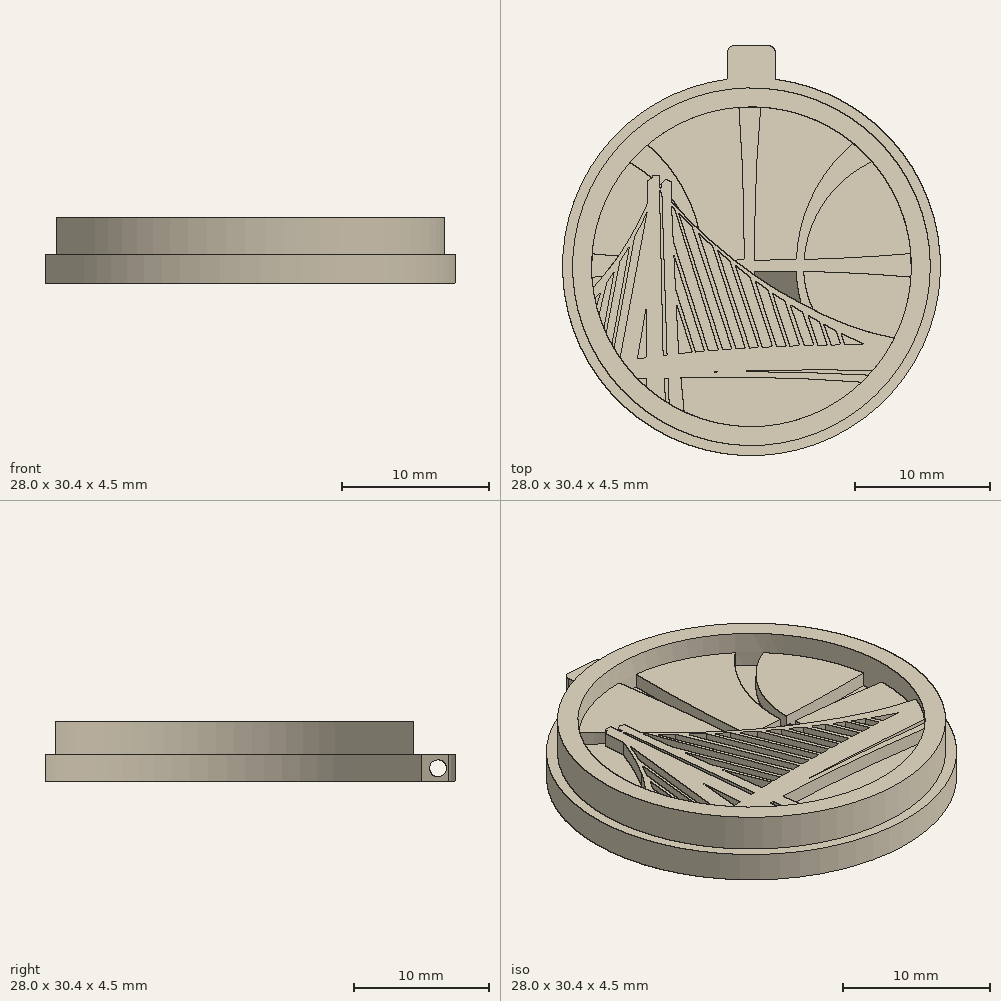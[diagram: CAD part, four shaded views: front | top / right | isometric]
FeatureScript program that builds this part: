
annotation { "Feature Type Name" : "Feature", "Feature Type Description" : "" }
export const myFeature = defineFeature(function(context is Context, id is Id, definition is map)
    precondition{}
    {
        {
            var Q0;
            Q0=qCreatedBy(makeId("Top.planeOp"),FACE);
            var sketch = newSketch(context, id + "F0", { "sketchPlane" : qUnion([Q0])});
            skCircle(sketch, "E0", {"center": v(0, 0) * mm, "radius": 12.5 * mm});
            skCircle(sketch, "E1", {"center": v(0, 0) * mm, "radius": 14 * mm});
            skSolve(sketch);
        }
        {
            var Q0;
            Q0 = qSketchRegion(id + "F0", true);
            var Q1;
            Q1=makeQuery(id+"F0.imprint","IMPRINT",FACE,{"disambiguationData":[TD([[makeQuery(id+"F0.imprint","IMPRINT",EDGE,{"derivedFrom":sQuery(id+"F0.wireOp",EDGE,"E0")}),1.0]])]});
            extrude(context, id + "F1", {"entities" : qUnion([Q0, Q1]), "depth" : 2 * mm, "offsetDistance" : 25 * mm});
        }
        {
            var Q0;
            Q0=makeQuery(id+"F1.opExtrude","CAP_FACE",FACE,{"disambiguationData":[OSD([sQuery(id+"F0.wireOp",EDGE,"E1")])],"isStart":false});
            var sketch = newSketch(context, id + "F2", { "sketchPlane" : qUnion([Q0])});
            skCircle(sketch, "E2", {"center": v(0, 0) * mm, "radius": 11.85 * mm});
            skArc(sketch, "E3", {"start": v(-0.54, 0.5) * mm, "mid": v(-0.63, 6.16) * mm, "end": v(-0.93, 11.81) * mm});
            skArc(sketch, "E4", {"start": v(0.69, 11.83) * mm, "mid": v(0.32, 6.17) * mm, "end": v(0.24, 0.5) * mm});
            skArc(sketch, "E5", {"start": v(0.24, 0.5) * mm, "mid": v(1.78, 0.5) * mm, "end": v(3.32, 0.52) * mm});
            skArc(sketch, "E6", {"start": v(11.82, -0.77) * mm, "mid": v(7.85, -0.49) * mm, "end": v(3.86, -0.34) * mm});
            skArc(sketch, "E7", {"start": v(8.94, 7.78) * mm, "mid": v(5.45, 4.83) * mm, "end": v(3.9, 0.54) * mm});
            skArc(sketch, "E8", {"start": v(7.55, 9.13) * mm, "mid": v(4.52, 5.28) * mm, "end": v(3.32, 0.52) * mm});
            skArc(sketch, "E9", {"start": v(-3.88, 2.71) * mm, "mid": v(-5.28, 6.17) * mm, "end": v(-7.68, 9.02) * mm});
            skArc(sketch, "E10", {"start": v(-5.28, 4.12) * mm, "mid": v(-5.59, 4.6) * mm, "end": v(-5.92, 5.04) * mm});
            skPoint(sketch, "E10.startSnap0", {"position": v(-5.28, 6.17) * mm});
            skArc(sketch, "E11", {"start": v(-5.28, 4.12) * mm, "mid": v(-3.36, 2.23) * mm, "end": v(-1.3, 0.5) * mm});
            skLineSegment(sketch, "E12", {"start": v(-0.54, 0.5) * mm, "end": v(-1.3, 0.5) * mm});
            skLineSegment(sketch, "E13", {"start": v(-11.82, -0.77) * mm, "end": v(-11, -0.73) * mm});
            skLineSegment(sketch, "E14", {"start": v(-11.81, 0.96) * mm, "end": v(-9.83, 0.79) * mm});
            skArc(sketch, "E15", {"start": v(-11, -0.73) * mm, "mid": v(-10.4, 0.02) * mm, "end": v(-9.83, 0.79) * mm});
            skLineSegment(sketch, "E16", {"start": v(-7.36, 6.55) * mm, "end": v(-7.36, 6.75) * mm});
            skLineSegment(sketch, "E17", {"start": v(-7.36, 6.75) * mm, "end": v(-6.8, 6.75) * mm});
            skLineSegment(sketch, "E18", {"start": v(-6.8, 6.75) * mm, "end": v(-6.8, 6.03) * mm});
            skLineSegment(sketch, "E19", {"start": v(-6.8, 6.03) * mm, "end": v(-6.32, 6.45) * mm});
            skLineSegment(sketch, "E20", {"start": v(-6.32, 6.45) * mm, "end": v(-5.92, 6.3) * mm});
            skLineSegment(sketch, "E21", {"start": v(-5.92, 6.3) * mm, "end": v(-5.92, 5.04) * mm});
            skArc(sketch, "E22.trimOffspring", {"start": v(-7.36, 6.55) * mm, "mid": v(-8.16, 7.17) * mm, "end": v(-9, 7.7) * mm});
            skArc(sketch, "E23", {"start": v(3.86, -0.34) * mm, "mid": v(4.07, -1.78) * mm, "end": v(4.56, -3.14) * mm});
            skArc(sketch, "E24", {"start": v(3.33, -0.33) * mm, "mid": v(3.42, -1.53) * mm, "end": v(3.67, -2.7) * mm});
            skArc(sketch, "E25", {"start": v(3.67, -2.7) * mm, "mid": v(4.1, -2.94) * mm, "end": v(4.56, -3.14) * mm});
            skArc(sketch, "E26.trimOffspring", {"start": v(3.9, 0.54) * mm, "mid": v(7.86, 0.7) * mm, "end": v(11.8, 0.97) * mm});
            skArc(sketch, "E27.trimOffspring", {"start": v(3.33, -0.33) * mm, "mid": v(1.79, -0.32) * mm, "end": v(0.24, -0.34) * mm});
            skArc(sketch, "E28", {"start": v(-1.3, 0.5) * mm, "mid": v(-0.54, -0.1) * mm, "end": v(0.24, -0.63) * mm});
            skLineSegment(sketch, "E29", {"start": v(0.24, -0.34) * mm, "end": v(0.24, -0.63) * mm});
            skSolve(sketch);
        }
        {
            var Q0;
            {var subQ1=sQuery(id+"F2.wireOp",EDGE,"E3");Q0=makeQuery(id+"F2.imprint","IMPRINT",FACE,{"disambiguationData":[TD([[makeQuery(id+"F2.imprint","IMPRINT",EDGE,{"derivedFrom":subQ1}),1.0]])]});}
            var Q1;
            {var subQ0=sQuery(id+"F2.wireOp",EDGE,"E4");Q1=makeQuery(id+"F2.imprint","IMPRINT",FACE,{"disambiguationData":[TD([[makeQuery(id+"F2.imprint","IMPRINT",EDGE,{"derivedFrom":subQ0}),1.0]])]});}
            var Q2;
            {var subQ0=sQuery(id+"F2.wireOp",EDGE,"E7");Q2=makeQuery(id+"F2.imprint","IMPRINT",FACE,{"disambiguationData":[TD([[makeQuery(id+"F2.imprint","IMPRINT",EDGE,{"derivedFrom":subQ0}),1.0]])]});}
            var Q3;
            {var subQ6=sQuery(id+"F2.wireOp",EDGE,"E6");Q3=makeQuery(id+"F2.imprint","IMPRINT",FACE,{"disambiguationData":[TD([[makeQuery(id+"F2.imprint","IMPRINT",EDGE,{"derivedFrom":subQ6}),1.0]])]});}
            extrude(context, id + "F3", {"entities" : qUnion([Q0, Q1, Q2, Q3]), "operationType" : NewBodyOperationType.ADD, "depth" : 1 * mm, "offsetDistance" : 25 * mm});
        }
        {
            var Q0;
            Q0=makeQuery(id+"F1.opExtrude","CAP_FACE",FACE,{"disambiguationData":[OSD([sQuery(id+"F0.wireOp",EDGE,"E1")])],"isStart":false});
            var sketch = newSketch(context, id + "F4", { "sketchPlane" : qUnion([Q0])});
            skCircle(sketch, "E30.0", {"center": v(0, 0) * mm, "radius": 13.25 * mm});
            skCircle(sketch, "E31", {"center": v(0, 0) * mm, "radius": 11.85 * mm});
            skSolve(sketch);
        }
        {
            var Q0;
            Q0 = qSketchRegion(id + "F4", true);
            extrude(context, id + "F5", {"entities" : qUnion([Q0]), "operationType" : NewBodyOperationType.ADD, "depth" : 2 * mm, "offsetDistance" : 25 * mm});
        }
        {
            var Q0;
            Q0=makeQuery(id+"F3.opExtrude","CAP_FACE",FACE,{"disambiguationData":[OSD([sQuery(id+"F2.wireOp",EDGE,"E2"),sQuery(id+"F2.wireOp",EDGE,"E3"),sQuery(id+"F2.wireOp",EDGE,"E6"),sQuery(id+"F2.wireOp",EDGE,"E9"),sQuery(id+"F2.wireOp",EDGE,"E10"),sQuery(id+"F2.wireOp",EDGE,"E11"),sQuery(id+"F2.wireOp",EDGE,"E12"),sQuery(id+"F2.wireOp",EDGE,"E13"),sQuery(id+"F2.wireOp",EDGE,"E14"),sQuery(id+"F2.wireOp",EDGE,"E15"),sQuery(id+"F2.wireOp",EDGE,"E16"),sQuery(id+"F2.wireOp",EDGE,"E17"),sQuery(id+"F2.wireOp",EDGE,"E18"),sQuery(id+"F2.wireOp",EDGE,"E19"),sQuery(id+"F2.wireOp",EDGE,"E20"),sQuery(id+"F2.wireOp",EDGE,"E21"),sQuery(id+"F2.wireOp",EDGE,"E22.trimOffspring"),sQuery(id+"F2.wireOp",EDGE,"E23"),sQuery(id+"F2.wireOp",EDGE,"E24"),sQuery(id+"F2.wireOp",EDGE,"E25"),sQuery(id+"F2.wireOp",EDGE,"E27.trimOffspring"),sQuery(id+"F2.wireOp",EDGE,"E28"),sQuery(id+"F2.wireOp",EDGE,"E29")])],"isStart":false});
            var sketch = newSketch(context, id + "F6", { "sketchPlane" : qUnion([Q0])});
            skLineSegment(sketch, "E32", {"start": v(-7.81, -6.75) * mm, "end": v(-7.81, -3.1) * mm});
            skLineSegment(sketch, "E33", {"start": v(-7.81, -3.1) * mm, "end": v(-8.45, -6.81) * mm});
            skLineSegment(sketch, "E34", {"start": v(-8.45, -6.81) * mm, "end": v(-7.81, -6.75) * mm});
            skLineSegment(sketch, "E35", {"start": v(-11.48, -2.94) * mm, "end": v(-11.15, -1.87) * mm});
            skLineSegment(sketch, "E36", {"start": v(-11.15, -1.87) * mm, "end": v(-11.6, -2.39) * mm});
            skLineSegment(sketch, "E37", {"start": v(-11.3, -3.59) * mm, "end": v(-10.7, -1.17) * mm});
            skLineSegment(sketch, "E38", {"start": v(-10.7, -1.17) * mm, "end": v(-10.16, -0.36) * mm});
            skLineSegment(sketch, "E39", {"start": v(-10.16, -0.36) * mm, "end": v(-10.93, -4.58) * mm});
            skLineSegment(sketch, "E40", {"start": v(-11.74, -1.6) * mm, "end": v(-11, -0.73) * mm});
            skArc(sketch, "E41", {"start": v(-9.83, 0.79) * mm, "mid": v(-8.68, 2.68) * mm, "end": v(-7.7, 4.66) * mm});
            skLineSegment(sketch, "E42", {"start": v(-7.7, 4.66) * mm, "end": v(-7.7, 6.36) * mm});
            skLineSegment(sketch, "E43", {"start": v(-7.7, 6.36) * mm, "end": v(-7.36, 6.55) * mm});
            skLineSegment(sketch, "E44", {"start": v(-7.36, 6.55) * mm, "end": v(-7.36, 6.75) * mm});
            skLineSegment(sketch, "E45", {"start": v(-7.36, 6.75) * mm, "end": v(-6.8, 6.75) * mm});
            skLineSegment(sketch, "E46", {"start": v(-6.8, 6.75) * mm, "end": v(-6.8, 5.88) * mm});
            skLineSegment(sketch, "E47", {"start": v(-6.8, 5.88) * mm, "end": v(-6.64, 5.71) * mm});
            skLineSegment(sketch, "E48", {"start": v(-6.64, 5.71) * mm, "end": v(-6.64, 6.18) * mm});
            skLineSegment(sketch, "E49", {"start": v(-6.64, 6.18) * mm, "end": v(-6.32, 6.45) * mm});
            skLineSegment(sketch, "E50", {"start": v(-6.32, 6.45) * mm, "end": v(-5.92, 6.3) * mm});
            skLineSegment(sketch, "E51", {"start": v(-5.92, 6.3) * mm, "end": v(-5.92, 4.8) * mm});
            skArc(sketch, "E52", {"start": v(-5.92, 4.8) * mm, "mid": v(-3.7, 2.55) * mm, "end": v(-1.3, 0.5) * mm});
            skArc(sketch, "E53", {"start": v(-1.3, 0.5) * mm, "mid": v(1.1, -1.23) * mm, "end": v(3.67, -2.7) * mm});
            skArc(sketch, "E54", {"start": v(3.67, -2.7) * mm, "mid": v(7.03, -4.28) * mm, "end": v(10.6, -5.3) * mm});
            skLineSegment(sketch, "E55", {"start": v(-6.47, -8.27) * mm, "end": v(-6.37, -10) * mm});
            skLineSegment(sketch, "E56", {"start": v(-6.47, -8.27) * mm, "end": v(-6.18, -8.27) * mm});
            skLineSegment(sketch, "E57", {"start": v(-6.18, -8.27) * mm, "end": v(-6.1, -10.16) * mm});
            skLineSegment(sketch, "E58", {"start": v(-7.8, -8.92) * mm, "end": v(-7.8, -8.3) * mm});
            skLineSegment(sketch, "E59", {"start": v(-7.8, -8.3) * mm, "end": v(-8.46, -8.3) * mm});
            skArc(sketch, "E60", {"start": v(8.2, -8.55) * mm, "mid": v(1.5, -8.21) * mm, "end": v(-5.23, -8.24) * mm});
            skArc(sketch, "E61", {"start": v(8.71, -8.03) * mm, "mid": v(2.98, -7.82) * mm, "end": v(-2.77, -7.8) * mm});
            skArc(sketch, "E62", {"start": v(9.03, -7.68) * mm, "mid": v(3.13, -7.65) * mm, "end": v(-2.77, -7.8) * mm});
            skArc(sketch, "E63", {"start": v(8.48, -5.79) * mm, "mid": v(7.7, -5.79) * mm, "end": v(6.91, -5.8) * mm});
            skArc(sketch, "E64", {"start": v(-5.92, 4.51) * mm, "mid": v(-5.8, 4.38) * mm, "end": v(-5.68, 4.26) * mm});
            skLineSegment(sketch, "E65", {"start": v(-5.92, 4.51) * mm, "end": v(-5.8, 1.88) * mm});
            skLineSegment(sketch, "E66", {"start": v(-6.26, -6.55) * mm, "end": v(-6.64, 5.45) * mm});
            skPoint(sketch, "E66.endSnap0", {"position": v(-6.64, 5.94) * mm});
            skLineSegment(sketch, "E67", {"start": v(-6.64, 5.45) * mm, "end": v(-6.82, 5.65) * mm});
            skLineSegment(sketch, "E68", {"start": v(-6.82, 5.65) * mm, "end": v(-6.55, -6.57) * mm});
            skLineSegment(sketch, "E69", {"start": v(-6.55, -6.57) * mm, "end": v(-6.26, -6.55) * mm});
            skLineSegment(sketch, "E70", {"start": v(-8.73, -6.88) * mm, "end": v(-7.78, -1.6) * mm});
            skLineSegment(sketch, "E71", {"start": v(-7.78, -1.6) * mm, "end": v(-7.7, 2.5) * mm});
            skLineSegment(sketch, "E72", {"start": v(-7.7, 2.5) * mm, "end": v(-9.56, -7) * mm});
            skLineSegment(sketch, "E73", {"start": v(-9.56, -7) * mm, "end": v(-8.73, -6.88) * mm});
            skArc(sketch, "E74", {"start": v(-9.76, 0.35) * mm, "mid": v(-9.39, 0.94) * mm, "end": v(-9.03, 1.54) * mm});
            skLineSegment(sketch, "E75", {"start": v(-7.73, 4.03) * mm, "end": v(-9.73, -6.77) * mm});
            skLineSegment(sketch, "E76", {"start": v(-10.18, -6.06) * mm, "end": v(-8.66, 2.18) * mm});
            skLineSegment(sketch, "E77", {"start": v(-9.03, 1.54) * mm, "end": v(-10.34, -5.79) * mm});
            skLineSegment(sketch, "E78", {"start": v(-9.76, 0.35) * mm, "end": v(-10.77, -4.95) * mm});
            skArc(sketch, "E79.trimOffspring", {"start": v(-8.66, 2.18) * mm, "mid": v(-8.18, 3.1) * mm, "end": v(-7.73, 4.03) * mm});
            skArc(sketch, "E80", {"start": v(-11.74, -1.6) * mm, "mid": v(-11.68, -2) * mm, "end": v(-11.6, -2.39) * mm});
            skLineSegment(sketch, "E81", {"start": v(-5.23, -8.24) * mm, "end": v(-4.99, -10.75) * mm});
            skLineSegment(sketch, "E82", {"start": v(-5.58, -2.66) * mm, "end": v(-4.39, -6.34) * mm});
            skLineSegment(sketch, "E83", {"start": v(-3.47, -6.26) * mm, "end": v(-5.75, 0.89) * mm});
            skLineSegment(sketch, "E84", {"start": v(-5.63, -1.66) * mm, "end": v(-4.16, -6.32) * mm});
            skLineSegment(sketch, "E85", {"start": v(-3.19, -6.24) * mm, "end": v(-5.8, 1.88) * mm});
            skLineSegment(sketch, "E86", {"start": v(-5.68, 4.26) * mm, "end": v(-2.45, -6.18) * mm});
            skLineSegment(sketch, "E87", {"start": v(-2.13, -6.16) * mm, "end": v(-5.4, 3.95) * mm});
            skLineSegment(sketch, "E88", {"start": v(-4.4, 2.94) * mm, "end": v(-1.45, -6.11) * mm});
            skLineSegment(sketch, "E89", {"start": v(-1.15, -6.09) * mm, "end": v(-3.9, 2.46) * mm});
            skLineSegment(sketch, "E90", {"start": v(-2.88, 1.52) * mm, "end": v(-0.46, -6.05) * mm});
            skLineSegment(sketch, "E91", {"start": v(-2.5, 1.2) * mm, "end": v(-0.14, -6.03) * mm});
            skLineSegment(sketch, "E92", {"start": v(0.54, -5.99) * mm, "end": v(-1.6, 0.42) * mm});
            skLineSegment(sketch, "E93", {"start": v(-1.2, 0.1) * mm, "end": v(0.81, -5.97) * mm});
            skLineSegment(sketch, "E94", {"start": v(1.87, -5.92) * mm, "end": v(0.26, -1.03) * mm});
            skLineSegment(sketch, "E95", {"start": v(1.56, -5.94) * mm, "end": v(-0.14, -0.73) * mm});
            skLineSegment(sketch, "E96", {"start": v(2.57, -5.9) * mm, "end": v(1.2, -1.7) * mm});
            skLineSegment(sketch, "E97", {"start": v(1.54, -1.94) * mm, "end": v(2.84, -5.88) * mm});
            skLineSegment(sketch, "E98", {"start": v(3.58, -5.86) * mm, "end": v(2.48, -2.56) * mm});
            skLineSegment(sketch, "E99", {"start": v(3.92, -5.85) * mm, "end": v(2.85, -2.8) * mm});
            skLineSegment(sketch, "E100", {"start": v(4.18, -3.6) * mm, "end": v(4.91, -5.82) * mm});
            skLineSegment(sketch, "E101", {"start": v(3.8, -3.37) * mm, "end": v(4.62, -5.83) * mm});
            skLineSegment(sketch, "E102", {"start": v(5.62, -5.8) * mm, "end": v(5.02, -4.07) * mm});
            skLineSegment(sketch, "E103", {"start": v(5.9, -5.8) * mm, "end": v(5.35, -4.25) * mm});
            skLineSegment(sketch, "E104", {"start": v(6.25, -4.73) * mm, "end": v(6.61, -5.8) * mm});
            skLineSegment(sketch, "E105", {"start": v(6.61, -4.91) * mm, "end": v(6.91, -5.8) * mm});
            skArc(sketch, "E106.trimOffspring", {"start": v(-3.9, 2.46) * mm, "mid": v(-3.4, 1.99) * mm, "end": v(-2.88, 1.52) * mm});
            skArc(sketch, "E107.trimOffspring", {"start": v(-2.5, 1.2) * mm, "mid": v(-2.05, 0.8) * mm, "end": v(-1.6, 0.42) * mm});
            skArc(sketch, "E108.trimOffspring", {"start": v(-5.4, 3.95) * mm, "mid": v(-4.9, 3.44) * mm, "end": v(-4.4, 2.94) * mm});
            skArc(sketch, "E109.trimOffspring", {"start": v(-1.2, 0.1) * mm, "mid": v(-0.68, -0.32) * mm, "end": v(-0.14, -0.73) * mm});
            skArc(sketch, "E110.trimOffspring", {"start": v(0.26, -1.03) * mm, "mid": v(0.73, -1.36) * mm, "end": v(1.2, -1.7) * mm});
            skArc(sketch, "E111.trimOffspring", {"start": v(1.54, -1.94) * mm, "mid": v(2, -2.25) * mm, "end": v(2.48, -2.56) * mm});
            skArc(sketch, "E112.trimOffspring", {"start": v(4.18, -3.6) * mm, "mid": v(4.6, -3.84) * mm, "end": v(5.02, -4.07) * mm});
            skArc(sketch, "E113.trimOffspring", {"start": v(2.85, -2.8) * mm, "mid": v(3.32, -3.08) * mm, "end": v(3.8, -3.37) * mm});
            skArc(sketch, "E114.trimOffspring", {"start": v(5.35, -4.25) * mm, "mid": v(5.8, -4.5) * mm, "end": v(6.25, -4.73) * mm});
            skArc(sketch, "E115.trimOffspring", {"start": v(6.61, -4.91) * mm, "mid": v(7.54, -5.36) * mm, "end": v(8.48, -5.79) * mm});
            skArc(sketch, "E116.trimOffspring", {"start": v(6.61, -5.8) * mm, "mid": v(6.26, -5.8) * mm, "end": v(5.9, -5.8) * mm});
            skArc(sketch, "E117.trimOffspring", {"start": v(5.62, -5.8) * mm, "mid": v(5.27, -5.81) * mm, "end": v(4.91, -5.82) * mm});
            skArc(sketch, "E118.trimOffspring", {"start": v(4.62, -5.83) * mm, "mid": v(4.27, -5.84) * mm, "end": v(3.92, -5.85) * mm});
            skArc(sketch, "E119.trimOffspring", {"start": v(3.58, -5.86) * mm, "mid": v(3.21, -5.87) * mm, "end": v(2.84, -5.88) * mm});
            skArc(sketch, "E120.trimOffspring", {"start": v(1.56, -5.94) * mm, "mid": v(1.19, -5.95) * mm, "end": v(0.81, -5.97) * mm});
            skArc(sketch, "E121.trimOffspring", {"start": v(2.57, -5.9) * mm, "mid": v(2.22, -5.9) * mm, "end": v(1.87, -5.92) * mm});
            skArc(sketch, "E122.trimOffspring", {"start": v(-2.45, -6.18) * mm, "mid": v(-2.82, -6.21) * mm, "end": v(-3.19, -6.24) * mm});
            skArc(sketch, "E123.trimOffspring", {"start": v(-1.45, -6.11) * mm, "mid": v(-1.79, -6.13) * mm, "end": v(-2.13, -6.16) * mm});
            skArc(sketch, "E124.trimOffspring", {"start": v(-3.47, -6.26) * mm, "mid": v(-3.81, -6.3) * mm, "end": v(-4.16, -6.32) * mm});
            skArc(sketch, "E125.trimOffspring", {"start": v(0.54, -5.99) * mm, "mid": v(0.2, -6) * mm, "end": v(-0.14, -6.03) * mm});
            skArc(sketch, "E126.trimOffspring", {"start": v(-0.46, -6.05) * mm, "mid": v(-0.8, -6.07) * mm, "end": v(-1.15, -6.09) * mm});
            skArc(sketch, "E127.trimOffspring", {"start": v(-4.39, -6.34) * mm, "mid": v(-4.9, -6.4) * mm, "end": v(-5.4, -6.44) * mm});
            skLineSegment(sketch, "E128.trimOffspring", {"start": v(-5.58, -2.66) * mm, "end": v(-5.4, -6.44) * mm});
            skLineSegment(sketch, "E129.trimOffspring", {"start": v(-5.75, 0.89) * mm, "end": v(-5.63, -1.66) * mm});
            skArc(sketch, "E130.trimOffspring", {"start": v(8.2, -8.55) * mm, "mid": v(8.46, -8.3) * mm, "end": v(8.71, -8.03) * mm});
            skArc(sketch, "E131.trimOffspring", {"start": v(9.03, -7.68) * mm, "mid": v(9.88, -6.54) * mm, "end": v(10.6, -5.3) * mm});
            skArc(sketch, "E132.trimOffspring", {"start": v(-6.1, -10.16) * mm, "mid": v(-5.55, -10.47) * mm, "end": v(-4.99, -10.75) * mm});
            skArc(sketch, "E133.trimOffspring", {"start": v(-7.8, -8.92) * mm, "mid": v(-7.1, -9.48) * mm, "end": v(-6.37, -10) * mm});
            skArc(sketch, "E134.trimOffspring", {"start": v(-11.48, -2.94) * mm, "mid": v(-11.4, -3.27) * mm, "end": v(-11.3, -3.59) * mm});
            skArc(sketch, "E135.trimOffspring", {"start": v(-10.93, -4.58) * mm, "mid": v(-10.85, -4.76) * mm, "end": v(-10.77, -4.95) * mm});
            skArc(sketch, "E136.trimOffspring", {"start": v(-10.34, -5.79) * mm, "mid": v(-10.26, -5.92) * mm, "end": v(-10.18, -6.06) * mm});
            skArc(sketch, "E137.trimOffspring", {"start": v(-9.73, -6.77) * mm, "mid": v(-9.13, -7.56) * mm, "end": v(-8.46, -8.3) * mm});
            skArc(sketch, "E138", {"start": v(-11, -0.73) * mm, "mid": v(-10.4, 0.02) * mm, "end": v(-9.83, 0.79) * mm});
            skSolve(sketch);
        }
        {
            var Q0;
            Q0 = qSketchRegion(id + "F6", true);
            extrude(context, id + "F7", {"entities" : qUnion([Q0]), "depth" : 1 * mm, "offsetDistance" : 25 * mm});
        }
        {
            var Q0;
            Q0=makeQuery(id+"F1.opExtrude","CAP_FACE",FACE,{"disambiguationData":[OSD([sQuery(id+"F0.wireOp",EDGE,"E1")])],"isStart":false});
            var sketch = newSketch(context, id + "F8", { "sketchPlane" : qUnion([Q0])});
            skLineSegment(sketch, "E139.top", {"start": v(-1.75, 16.4) * mm, "end": v(1.75, 16.4) * mm});
            skLineSegment(sketch, "E139.left", {"start": v(-1.75, 13.9) * mm, "end": v(-1.75, 16.4) * mm});
            skLineSegment(sketch, "E139.right", {"start": v(1.75, 13.9) * mm, "end": v(1.75, 16.4) * mm});
            skPoint(sketch, "E139.middle", {"position": v(0, 15.14) * mm});
            skLineSegment(sketch, "E140", {"start": v(0, 15.14) * mm, "end": v(0, 0) * mm, "construction": true});
            skArc(sketch, "E141", {"start": v(-1.75, 13.9) * mm, "mid": v(0, 13.87) * mm, "end": v(1.75, 13.9) * mm});
            skSolve(sketch);
        }
        {
            var Q0;
            Q0 = qSketchRegion(id + "F8", true);
            extrude(context, id + "F9", {"entities" : qUnion([Q0]), "operationType" : NewBodyOperationType.ADD, "oppositeDirection" : true, "depth" : 2 * mm, "offsetDistance" : 25 * mm});
        }
        {
            var Q0;
            Q0=makeQuery(id+"F9.opExtrude","SWEPT_EDGE",EDGE,{"disambiguationData":[OSD([sQuery(id+"F8.wireOp",EDGE,"E139.top"),sQuery(id+"F8.wireOp",EDGE,"E139.right")])]});
            var Q1;
            Q1=makeQuery(id+"F9.opExtrude","SWEPT_EDGE",EDGE,{"disambiguationData":[OSD([sQuery(id+"F0.wireOp",EDGE,"E1"),sQuery(id+"F8.wireOp",EDGE,"E139.right"),sQuery(id+"F8.wireOp",EDGE,"E141")])]});
            var Q2;
            Q2=makeQuery(id+"F9.opExtrude","SWEPT_EDGE",EDGE,{"disambiguationData":[OSD([sQuery(id+"F8.wireOp",EDGE,"E139.top"),sQuery(id+"F8.wireOp",EDGE,"E139.left")])]});
            var Q3;
            Q3=makeQuery(id+"F9.opExtrude","SWEPT_EDGE",EDGE,{"disambiguationData":[OSD([sQuery(id+"F0.wireOp",EDGE,"E1"),sQuery(id+"F8.wireOp",EDGE,"E139.left"),sQuery(id+"F8.wireOp",EDGE,"E141")])]});
            fillet(context, id + "F10", {"entities" : qUnion([Q0, Q1, Q2, Q3]), "radius" : .5 * mm, "tangentPropagation" : true, "allowEdgeOverflow" : false});
        }
        {
            var Q0;
            Q0=makeQuery(id+"F9.opExtrude","SWEPT_FACE",FACE,{"disambiguationData":[OSD([sQuery(id+"F8.wireOp",EDGE,"E139.right")])]});
            var sketch = newSketch(context, id + "F11", { "sketchPlane" : qUnion([Q0])});
            skCircle(sketch, "E142", {"center": v(15.1, 1) * mm, "radius": 0.62 * mm});
            skPoint(sketch, "E142.centerSnap0", {"position": v(14.32, 1) * mm});
            skPoint(sketch, "E142.centerSnap1", {"position": v(15.1, 2) * mm});
            skSolve(sketch);
        }
        {
            var Q0;
            Q0 = qSketchRegion(id + "F11", true);
            extrude(context, id + "F12", {"entities" : qUnion([Q0]), "operationType" : NewBodyOperationType.REMOVE, "oppositeDirection" : true, "depth" : 25 * mm, "offsetDistance" : 25 * mm, "hasSecondDirection" : true, "secondDirectionOppositeDirection" : false, "secondDirectionDepth" : 25 * mm});
        }
        {
            var Q0;
            Q0=makeQuery(id+"F5.opExtrude","CAP_FACE",FACE,{"disambiguationData":[OSD([sQuery(id+"F4.wireOp",EDGE,"E30.0"),sQuery(id+"F4.wireOp",EDGE,"E31")])],"isStart":false});
            var sketch = newSketch(context, id + "F13", { "sketchPlane" : qUnion([Q0])});
            skCircle(sketch, "E143.0", {"center": v(0, 0) * mm, "radius": 13.25 * mm});
            skCircle(sketch, "E144.0", {"center": v(0, 0) * mm, "radius": 11.85 * mm});
            skSolve(sketch);
        }
        {
            var Q0;
            Q0 = qSketchRegion(id + "F13", true);
            extrude(context, id + "F14", {"entities" : qUnion([Q0]), "operationType" : NewBodyOperationType.REMOVE, "oppositeDirection" : true, "depth" : 1 * mm, "offsetDistance" : 25 * mm});
        }
        {
            var Q0;
            {var subQ0=sQuery(id+"F2.wireOp",EDGE,"E2");Q0=makeQuery(id+"F14.boolean.opBoolean","MERGE",FACE,{"derivedFrom":[makeQuery(id+"F3.opExtrude","CAP_FACE",FACE,{"disambiguationData":[OSD([subQ0,sQuery(id+"F2.wireOp",EDGE,"E7"),sQuery(id+"F2.wireOp",EDGE,"E26.trimOffspring")])],"isStart":false}),makeQuery(id+"F3.opExtrude","CAP_FACE",FACE,{"disambiguationData":[OSD([subQ0,sQuery(id+"F2.wireOp",EDGE,"E4"),sQuery(id+"F2.wireOp",EDGE,"E5"),sQuery(id+"F2.wireOp",EDGE,"E8")])],"isStart":false}),makeQuery(id+"F3.opExtrude","CAP_FACE",FACE,{"disambiguationData":[OSD([subQ0,sQuery(id+"F2.wireOp",EDGE,"E3"),sQuery(id+"F2.wireOp",EDGE,"E6"),sQuery(id+"F2.wireOp",EDGE,"E9"),sQuery(id+"F2.wireOp",EDGE,"E10"),sQuery(id+"F2.wireOp",EDGE,"E11"),sQuery(id+"F2.wireOp",EDGE,"E12"),sQuery(id+"F2.wireOp",EDGE,"E13"),sQuery(id+"F2.wireOp",EDGE,"E14"),sQuery(id+"F2.wireOp",EDGE,"E15"),sQuery(id+"F2.wireOp",EDGE,"E16"),sQuery(id+"F2.wireOp",EDGE,"E17"),sQuery(id+"F2.wireOp",EDGE,"E18"),sQuery(id+"F2.wireOp",EDGE,"E19"),sQuery(id+"F2.wireOp",EDGE,"E20"),sQuery(id+"F2.wireOp",EDGE,"E21"),sQuery(id+"F2.wireOp",EDGE,"E22.trimOffspring"),sQuery(id+"F2.wireOp",EDGE,"E23"),sQuery(id+"F2.wireOp",EDGE,"E24"),sQuery(id+"F2.wireOp",EDGE,"E25"),sQuery(id+"F2.wireOp",EDGE,"E27.trimOffspring"),sQuery(id+"F2.wireOp",EDGE,"E28"),sQuery(id+"F2.wireOp",EDGE,"E29")])],"isStart":false}),makeQuery(id+"F14.opExtrude","CAP_FACE",FACE,{"disambiguationData":[OSD([sQuery(id+"F13.wireOp",EDGE,"E143.0"),sQuery(id+"F13.wireOp",EDGE,"E144.0")])],"isStart":false})]});}
            var sketch = newSketch(context, id + "F15", { "sketchPlane" : qUnion([Q0])});
            skCircle(sketch, "E145.0", {"center": v(0, 0) * mm, "radius": 13.25 * mm});
            skCircle(sketch, "E146", {"center": v(0, 0) * mm, "radius": 11.85 * mm});
            skSolve(sketch);
        }
        {
            var Q0;
            Q0 = qSketchRegion(id + "F15", true);
            extrude(context, id + "F16", {"entities" : qUnion([Q0]), "operationType" : NewBodyOperationType.ADD, "depth" : 1.5 * mm, "offsetDistance" : 25 * mm});
        }
    });
